# Revit family: Shower_Diverter-American_Standard-Serin-T064.700_Series
name_source: partatom
category: Plumbing Fixtures
revit_build: Autodesk Revit 2015 (Build: 20140606_1530(x64)
units: mm (PartAtom-declared; Revit-internal decimal feet)

## types (2) — shared parameters
ADA Compliant = Yes
Assembly Code = D2010710
CW Connection = Yes
CWFU = 3
Cold Water Connection Diameter = 1/2"
Cold Water Connection Radius = 1/4"
Default Elevation = 46"
Description = Serin Diverter Valve Trim Kit
HW Connection = Yes
HWFU = 3
Height = 2 1/8"
Hot Water Connection Diameter = 1/2"
Hot Water Connection Radius = 1/4"
Installation Type = Wall Mounted
Length = 2 1/8"
Manufacturer = American Standard
Price = Prices may vary. Please consult Manufacturer Representative for most up-to-date price list.
Product Documentation Link = https://www.americanstandard-us.com
Product Page URL = https://www.americanstandard-us.com
URL = http://www.americanstandard-us.com
Vent Connection = No
WFU = 4
Warranty Information = 1 Year Limited
Waste Connection = No
Width = 2 5/8"

## per-type parameters (varying)
| type | Material |
| T064.700.002 | Brass-American Standard-002-Polished Chrome |
| T064.700.295 | Brass-American Standard-295-Brushed Nickel |

note: column(s) folded — value = type name in every type: Model

## geometry (parser evidence)
native form markers: Sweep x4
no freeform markers — native parametric forms only
